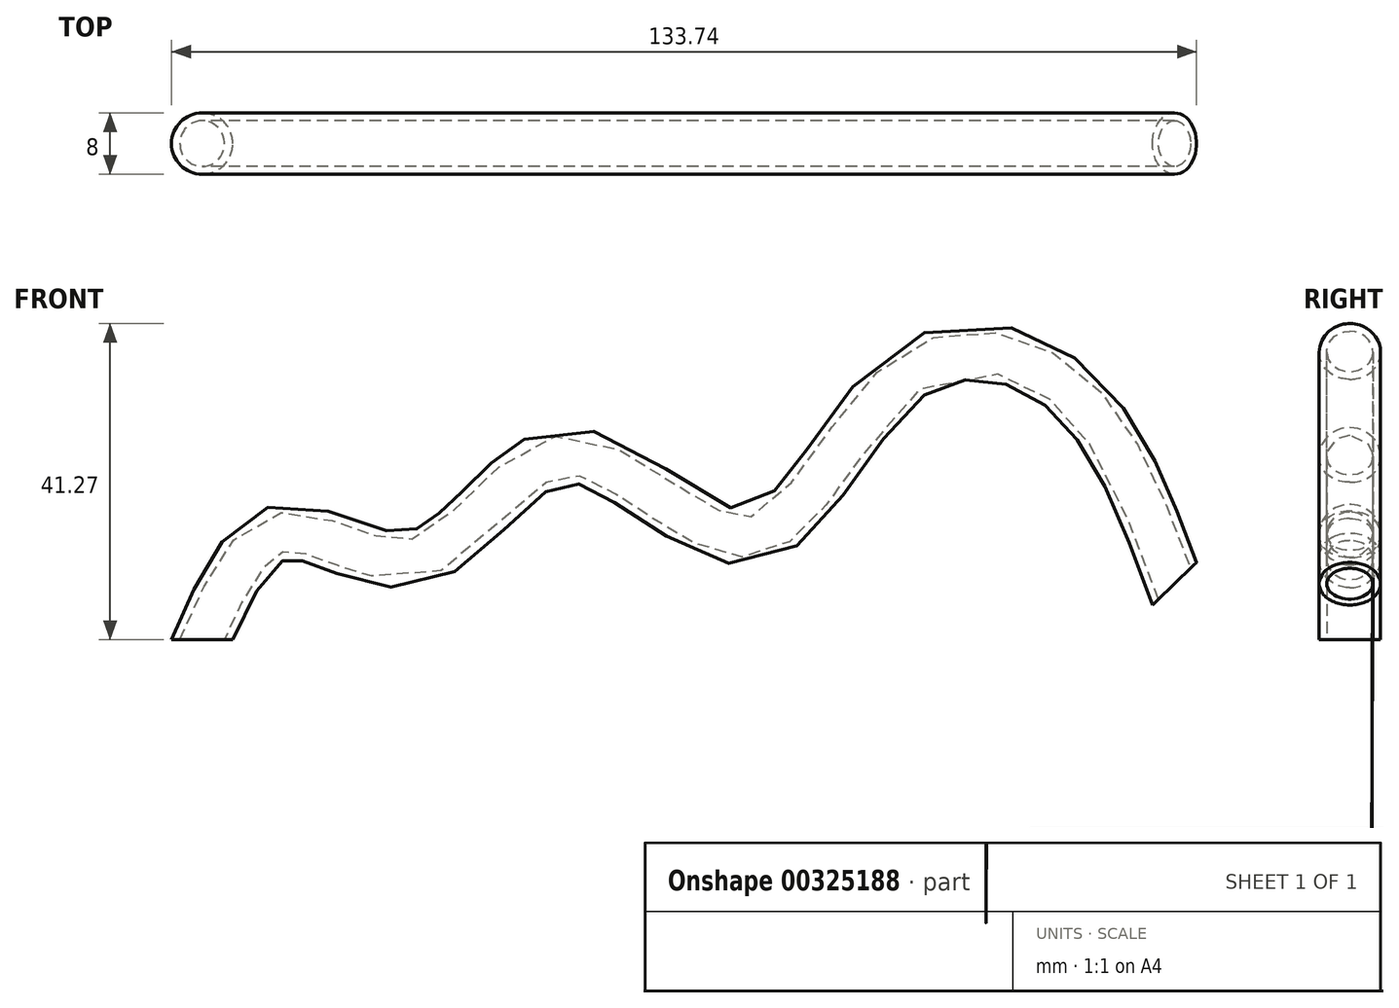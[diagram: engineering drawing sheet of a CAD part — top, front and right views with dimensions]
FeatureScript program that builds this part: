
annotation { "Feature Type Name" : "Feature", "Feature Type Description" : "" }
export const myFeature = defineFeature(function(context is Context, id is Id, definition is map)
    precondition{}
    {
        {
            var Q0;
            Q0=qCreatedBy(makeId("Front.planeOp"),FACE);
            var sketch = newSketch(context, id + "F0", { "sketchPlane" : qUnion([Q0])});
            skFitSpline(sketch, "E0", {"points": [v(-65.7, 0) * mm, v(-55.08, 13.84) * mm, v(-37.39, 10.84) * mm, v(-18.33, 23.9) * mm, v(5.63, 13.56) * mm, v(26.04, 34.53) * mm, v(46.46, 33.44) * mm, v(61.16, 7.3) * mm], "startDerivative": vector(70.06, 159.23) * mm, "endDerivative": vector(70.1, -190.42) * mm});
            skSolve(sketch);
        }
        {
            var Q0;
            Q0=qCreatedBy(makeId("Top.planeOp"),FACE);
            var sketch = newSketch(context, id + "F1", { "sketchPlane" : qUnion([Q0])});
            skCircle(sketch, "E1", {"center": v(-65.7, 0) * mm, "radius": 4 * mm});
            skSolve(sketch);
        }
        {
            var Q0;
            Q0=makeQuery(id+"F1.imprint","IMPRINT",FACE,{"disambiguationData":[TD([[makeQuery(id+"F1.imprint","IMPRINT",EDGE,{"derivedFrom":sQuery(id+"F1.wireOp",EDGE,"E1")}),1.0]])]});
            var Q1;
            Q1=sQuery(id+"F0.wireOp",EDGE,"E0");
            sweep(context, id + "F2", {"profiles" : qUnion([Q0]), "path" : qUnion([Q1])});
        }
        {
            var Q0;
            Q0=makeQuery(id+"F2.opSweep","CAP_FACE",FACE,{"disambiguationData":[OSD([sQuery(id+"F0.wireOp",VERTEX,"E0.start"),sQuery(id+"F1.wireOp",EDGE,"E1")])],"isStart":true});
            var Q1;
            Q1=makeQuery(id+"F2.opSweep","CAP_FACE",FACE,{"disambiguationData":[OSD([sQuery(id+"F0.wireOp",VERTEX,"E0.end"),sQuery(id+"F1.wireOp",EDGE,"E1")])],"isStart":false});
            shell(context, id + "F3", {"entities" : qUnion([Q0, Q1]), "thickness" : 1 * mm});
        }
    });
